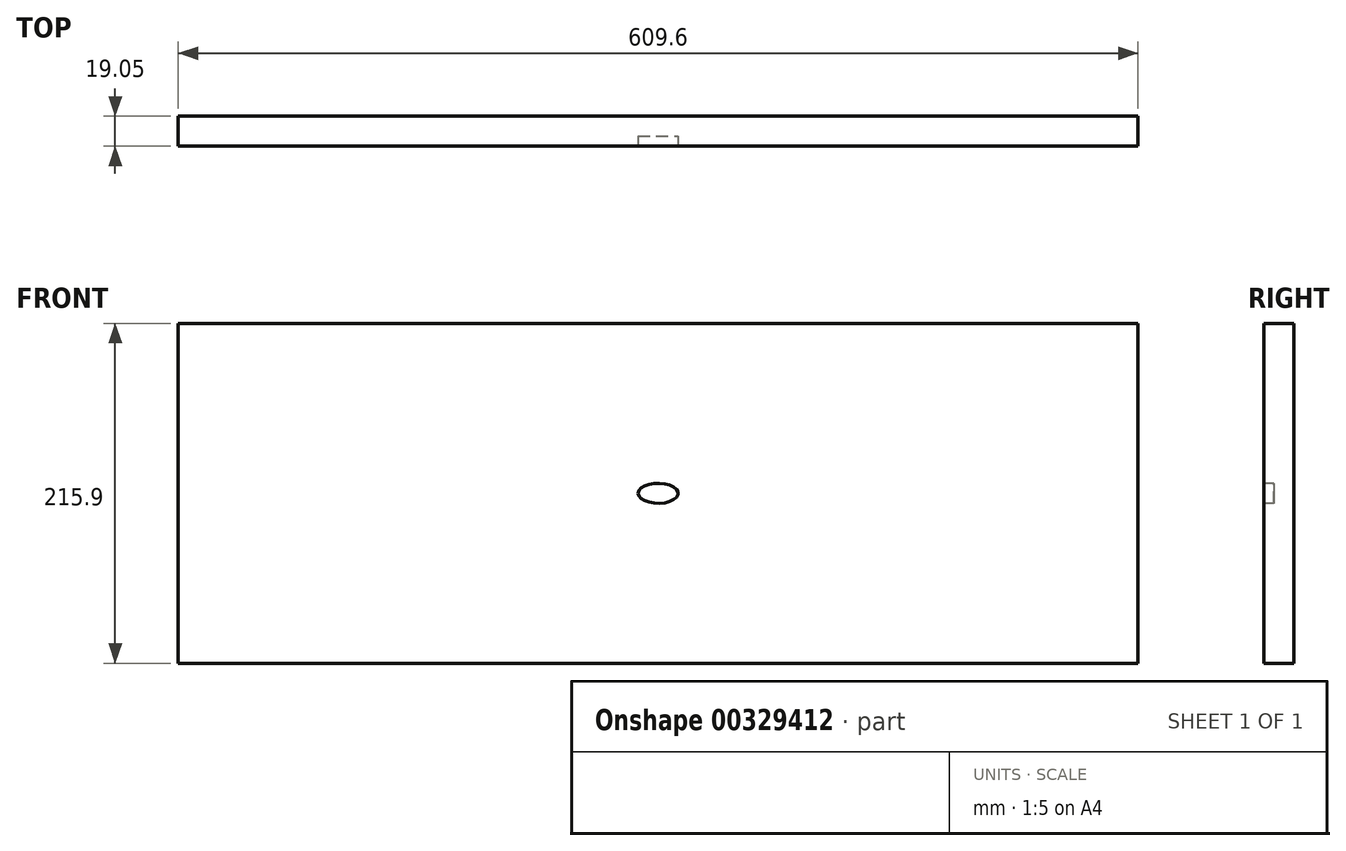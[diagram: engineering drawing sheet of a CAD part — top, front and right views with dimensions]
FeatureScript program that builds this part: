
annotation { "Feature Type Name" : "Feature", "Feature Type Description" : "" }
export const myFeature = defineFeature(function(context is Context, id is Id, definition is map)
    precondition{}
    {
        {
            var Q0;
            Q0=qCreatedBy(makeId("Front.planeOp"),FACE);
            var sketch = newSketch(context, id + "F0", { "sketchPlane" : qUnion([Q0])});
            skLineSegment(sketch, "E0.bottom", {"start": v(304.8, -107.95) * mm, "end": v(-304.8, -107.95) * mm});
            skLineSegment(sketch, "E0.top", {"start": v(304.8, 107.95) * mm, "end": v(-304.8, 107.95) * mm});
            skLineSegment(sketch, "E0.left", {"start": v(304.8, -107.95) * mm, "end": v(304.8, 107.95) * mm});
            skLineSegment(sketch, "E0.right", {"start": v(-304.8, -107.95) * mm, "end": v(-304.8, 107.95) * mm});
            skPoint(sketch, "E0.middle", {"position": v(0, 0) * mm});
            skSolve(sketch);
        }
        {
            var Q0;
            Q0 = qSketchRegion(id + "F0", true);
            extrude(context, id + "F1", {"entities" : qUnion([Q0]), "depth" : 19.05 * mm});
        }
        {
            var Q0;
            Q0=makeQuery(id+"F1.opExtrude","CAP_FACE",FACE,{"disambiguationData":[OSD([sQuery(id+"F0.wireOp",EDGE,"E0.bottom"),sQuery(id+"F0.wireOp",EDGE,"E0.top"),sQuery(id+"F0.wireOp",EDGE,"E0.left"),sQuery(id+"F0.wireOp",EDGE,"E0.right")])],"isStart":false});
            var sketch = newSketch(context, id + "F2", { "sketchPlane" : qUnion([Q0])});
            skEllipse(sketch, "E1", {"center": v(0, 0) * mm, "majorRadius": 6.35 * mm, "minorRadius": 12.7 * mm, "majorAxis": v(0, 1)});
            skSolve(sketch);
        }
        {
            var Q0;
            Q0 = qSketchRegion(id + "F2", true);
            extrude(context, id + "F3", {"entities" : qUnion([Q0]), "operationType" : NewBodyOperationType.REMOVE, "oppositeDirection" : true, "depth" : 6.35 * mm});
        }
    });
